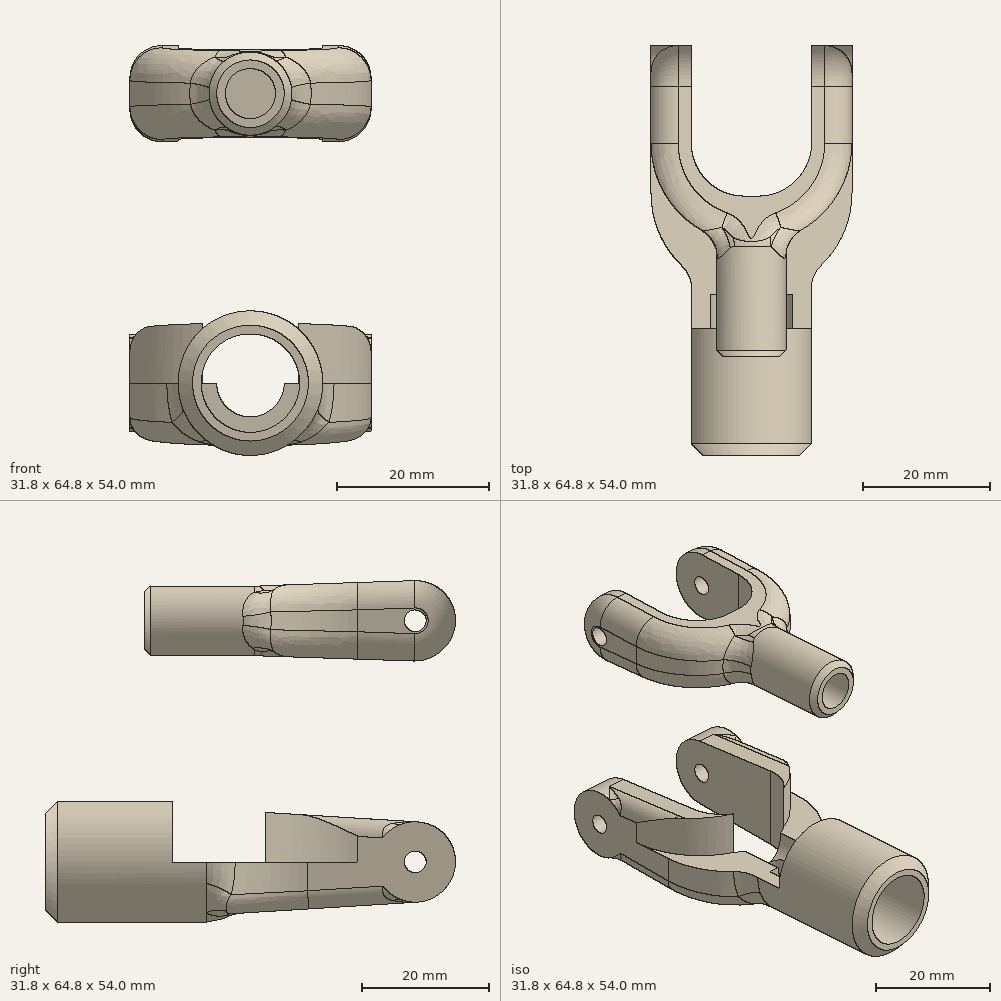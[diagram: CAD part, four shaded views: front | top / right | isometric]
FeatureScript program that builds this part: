
annotation { "Feature Type Name" : "Feature", "Feature Type Description" : "" }
export const myFeature = defineFeature(function(context is Context, id is Id, definition is map)
    precondition{}
    {
        {
            var Q0;
            Q0=qCreatedBy(makeId("Right.planeOp"),FACE);
            var sketch = newSketch(context, id + "F0", { "sketchPlane" : qUnion([Q0])});
            skArc(sketch, "E0", {"start": v(0.4, -6.34) * mm, "mid": v(6.35, 0) * mm, "end": v(0.4, 6.34) * mm});
            skLineSegment(sketch, "E1", {"start": v(0.4, 6.34) * mm, "end": v(-50.8, 9.52) * mm});
            skLineSegment(sketch, "E2", {"start": v(-50.8, 9.52) * mm, "end": v(-50.8, -9.52) * mm});
            skLineSegment(sketch, "E3", {"start": v(-50.8, -9.52) * mm, "end": v(0.4, -6.34) * mm});
            skCircle(sketch, "E4", {"center": v(0, 0) * mm, "radius": 1.71 * mm});
            skSolve(sketch);
        }
        {
            var Q0;
            Q0=qSketchRegion(id+"F0",true);
            extrude(context, id + "F1", {"entities" : qUnion([Q0]), "depth" : 15.88 * mm, "hasSecondDirection" : true, "secondDirectionOppositeDirection" : true, "secondDirectionDepth" : 15.88 * mm});
        }
        {
            var Q0;
            Q0=qCreatedBy(makeId("Top.planeOp"),FACE);
            var sketch = newSketch(context, id + "F2", { "sketchPlane" : qUnion([Q0])});
            skLineSegment(sketch, "E5.bottom", {"start": v(-9.52, 7.24) * mm, "end": v(9.52, 7.24) * mm});
            skLineSegment(sketch, "E5.top", {"start": v(-1.14, -25.4) * mm, "end": v(1.14, -25.4) * mm});
            skLineSegment(sketch, "E5.left", {"start": v(-9.52, 7.24) * mm, "end": v(-9.52, -17.02) * mm});
            skLineSegment(sketch, "E5.right", {"start": v(9.53, 7.24) * mm, "end": v(9.53, -17.02) * mm});
            skPoint(sketch, "E6.visualSharp", {"position": v(-9.52, -25.4) * mm});
            skArc(sketch, "E6.filletArc", {"start": v(-9.52, -17.02) * mm, "mid": v(-7.07, -22.94) * mm, "end": v(-1.14, -25.4) * mm});
            skPoint(sketch, "E7.visualSharp", {"position": v(9.52, -25.4) * mm});
            skArc(sketch, "E7.filletArc", {"start": v(1.14, -25.4) * mm, "mid": v(7.07, -22.94) * mm, "end": v(9.52, -17.02) * mm});
            skArc(sketch, "E8", {"start": v(-15.88, -17.02) * mm, "mid": v(0, -32.9) * mm, "end": v(15.88, -17.02) * mm});
            skLineSegment(sketch, "E9", {"start": v(-15.88, -17.02) * mm, "end": v(-15.88, -50.8) * mm});
            skLineSegment(sketch, "E10", {"start": v(-15.88, -50.8) * mm, "end": v(15.88, -50.8) * mm});
            skLineSegment(sketch, "E11", {"start": v(15.88, -50.8) * mm, "end": v(15.88, -17.02) * mm});
            skSolve(sketch);
        }
        {
            var Q0;
            Q0=qSketchRegion(id+"F2",true);
            extrude(context, id + "F3", {"entities" : qUnion([Q0]), "operationType" : NewBodyOperationType.REMOVE, "endBound" : BoundingType.THROUGH_ALL, "oppositeDirection" : true, "depth" : 25.4 * mm, "hasSecondDirection" : true, "secondDirectionBound" : BoundingType.THROUGH_ALL, "secondDirectionOppositeDirection" : false, "secondDirectionDepth" : 25.4 * mm});
        }
        {
            var Q0;
            Q0=qCreatedBy(makeId("Right.planeOp"),FACE);
            var sketch = newSketch(context, id + "F4", { "sketchPlane" : qUnion([Q0])});
            skLineSegment(sketch, "E12", {"start": v(0, 0) * mm, "end": v(-108.54, 0) * mm, "construction": true});
            skSolve(sketch);
        }
        {
            var Q0;
            Q0=qCreatedBy(makeId("Right.planeOp"),FACE);
            var sketch = newSketch(context, id + "F5", { "sketchPlane" : qUnion([Q0])});
            skLineSegment(sketch, "E13", {"start": v(-25.4, 0) * mm, "end": v(-25.4, 7.94) * mm});
            skLineSegment(sketch, "E14", {"start": v(-58.42, 9.53) * mm, "end": v(-58.42, 0) * mm});
            skLineSegment(sketch, "E15", {"start": v(-58.42, 0) * mm, "end": v(-25.4, 0) * mm});
            skLineSegment(sketch, "E16", {"start": v(-25.4, 7.94) * mm, "end": v(-33.02, 9.53) * mm});
            skLineSegment(sketch, "E17", {"start": v(-33.02, 9.53) * mm, "end": v(-58.42, 9.53) * mm});
            skSolve(sketch);
        }
        {
            var Q0;
            Q0=qSketchRegion(id+"F5",true);
            var Q1;
            Q1=sQuery(id+"F4.wireOp",EDGE,"E12");
            revolve(context, id + "F6", {"operationType" : NewBodyOperationType.ADD, "entities" : qUnion([Q0]), "axis" : qUnion([Q1]), "revolveType" : RevolveType.FULL});
        }
        {
            var Q0;
            Q0=qCreatedBy(makeId("Right.planeOp"),FACE);
            var sketch = newSketch(context, id + "F7", { "sketchPlane" : qUnion([Q0])});
            skLineSegment(sketch, "E18", {"start": v(-58.42, 6.48) * mm, "end": v(-33.02, 6.48) * mm});
            skLineSegment(sketch, "E19", {"start": v(-33.02, 6.48) * mm, "end": v(-33.02, 4.45) * mm});
            skLineSegment(sketch, "E20", {"start": v(-33.02, 4.45) * mm, "end": v(-23.5, 4.45) * mm});
            skLineSegment(sketch, "E21", {"start": v(-23.5, 4.45) * mm, "end": v(-23.5, 0) * mm});
            skLineSegment(sketch, "E22", {"start": v(-58.42, 6.48) * mm, "end": v(-58.42, 0) * mm});
            skLineSegment(sketch, "E23", {"start": v(-58.42, 0) * mm, "end": v(-23.5, 0) * mm});
            skSolve(sketch);
        }
        {
            var Q0;
            Q0=qSketchRegion(id+"F7",true);
            var Q1;
            Q1=sQuery(id+"F4.wireOp",EDGE,"E12");
            revolve(context, id + "F8", {"operationType" : NewBodyOperationType.REMOVE, "entities" : qUnion([Q0]), "axis" : qUnion([Q1]), "revolveType" : RevolveType.FULL, "oppositeDirection" : true});
        }
        {
            var Q0;
            {var subQ0=sQuery(id+"F0.wireOp",EDGE,"E1");var subQ1=makeQuery(id+"F1.opExtrude","SWEPT_FACE",FACE,{"disambiguationData":[OSD([subQ0])]});var subQ2=makeQuery(id+"F3.opExtrude","SWEPT_FACE",FACE,{"disambiguationData":[OSD([sQuery(id+"F2.wireOp",EDGE,"E8")])]});Q0=makeQuery(id+"F6.boolean.opBoolean","SPLIT",EDGE,{"disambiguationData":[TD([makeQuery(id+"F1.opExtrude","CAP_FACE",FACE,{"disambiguationData":[OSD([sQuery(id+"F0.wireOp",EDGE,"E0"),subQ0,sQuery(id+"F0.wireOp",EDGE,"E2"),sQuery(id+"F0.wireOp",EDGE,"E3"),sQuery(id+"F0.wireOp",EDGE,"E4")])],"isStart":true})])],"derivedFrom":makeQuery(id+"F3.boolean.opBoolean","INTERSECT",EDGE,{"derivedFrom":[subQ1,subQ2]})});}
            var Q1;
            {var subQ0=sQuery(id+"F0.wireOp",EDGE,"E1");var subQ1=makeQuery(id+"F1.opExtrude","SWEPT_FACE",FACE,{"disambiguationData":[OSD([subQ0])]});var subQ2=makeQuery(id+"F3.opExtrude","SWEPT_FACE",FACE,{"disambiguationData":[OSD([sQuery(id+"F2.wireOp",EDGE,"E8")])]});Q1=makeQuery(id+"F6.boolean.opBoolean","SPLIT",EDGE,{"disambiguationData":[TD([makeQuery(id+"F1.opExtrude","CAP_FACE",FACE,{"disambiguationData":[OSD([sQuery(id+"F0.wireOp",EDGE,"E0"),subQ0,sQuery(id+"F0.wireOp",EDGE,"E2"),sQuery(id+"F0.wireOp",EDGE,"E3"),sQuery(id+"F0.wireOp",EDGE,"E4")])],"isStart":false})])],"derivedFrom":makeQuery(id+"F3.boolean.opBoolean","INTERSECT",EDGE,{"derivedFrom":[subQ1,subQ2]})});}
            fillet(context, id + "F9", {"entities" : qUnion([Q0, Q1]), "radius" : 2.87 * mm, "tangentPropagation" : true, "allowEdgeOverflow" : false});
        }
        {
            var Q0;
            Q0=makeQuery(id+"F6.boolean.opBoolean","INTERSECT",EDGE,{"disambiguationData":[OD(1.0)],"derivedFrom":[makeQuery(id+"F3.boolean.opBoolean","COPY",FACE,{"derivedFrom":makeQuery(id+"F3.opExtrude","SWEPT_FACE",FACE,{"disambiguationData":[OSD([sQuery(id+"F2.wireOp",EDGE,"E8")])]})}),makeQuery(id+"F6.opRevolve","SWEPT_FACE",FACE,{"disambiguationData":[OSD([sQuery(id+"F5.wireOp",EDGE,"E16")])]})]});
            fillet(context, id + "F10", {"entities" : qUnion([Q0]), "radius" : 5.08 * mm, "tangentPropagation" : true, "allowEdgeOverflow" : false});
        }
        {
            var Q0;
            Q0=makeQuery(id+"F6.opRevolve","SWEPT_EDGE",EDGE,{"disambiguationData":[OSD([sQuery(id+"F5.wireOp",EDGE,"E14"),sQuery(id+"F5.wireOp",EDGE,"E17")])]});
            chamfer(context, id + "F11", {"entities" : qUnion([Q0]), "width" : 1.9 * mm, "tangentPropagation" : true});
        }
        {
            var Q0;
            Q0=qCreatedBy(makeId("Right.planeOp"),FACE);
            var sketch = newSketch(context, id + "F12", { "sketchPlane" : qUnion([Q0])});
            skCircle(sketch, "E24", {"center": v(0, 38.1) * mm, "radius": 1.71 * mm});
            skArc(sketch, "E25", {"start": v(-0.21, 31.75) * mm, "mid": v(6.35, 38.1) * mm, "end": v(-0.21, 44.45) * mm});
            skLineSegment(sketch, "E26", {"start": v(-0.21, 44.45) * mm, "end": v(-38.3, 43.18) * mm});
            skLineSegment(sketch, "E27", {"start": v(-38.3, 43.18) * mm, "end": v(-38.3, 33.02) * mm});
            skLineSegment(sketch, "E28", {"start": v(-38.3, 33.02) * mm, "end": v(-0.21, 31.75) * mm});
            skLineSegment(sketch, "E29", {"start": v(-60.22, 38.1) * mm, "end": v(0, 38.1) * mm, "construction": true});
            skSolve(sketch);
        }
        {
            var Q0;
            Q0=qSketchRegion(id+"F12",true);
            extrude(context, id + "F13", {"entities" : qUnion([Q0]), "depth" : 15.88 * mm, "hasSecondDirection" : true, "secondDirectionOppositeDirection" : true, "secondDirectionDepth" : 15.88 * mm});
        }
        {
            var Q0;
            Q0=qCreatedBy(makeId("Top.planeOp"),FACE);
            var sketch = newSketch(context, id + "F14", { "sketchPlane" : qUnion([Q0])});
            skLineSegment(sketch, "E30.bottom", {"start": v(-9.53, 7.96) * mm, "end": v(9.53, 7.96) * mm});
            skLineSegment(sketch, "E30.top", {"start": v(-1.14, -17.44) * mm, "end": v(1.14, -17.44) * mm});
            skLineSegment(sketch, "E30.left", {"start": v(-9.53, 7.96) * mm, "end": v(-9.53, -9.06) * mm});
            skLineSegment(sketch, "E30.right", {"start": v(9.53, 7.96) * mm, "end": v(9.53, -9.06) * mm});
            skPoint(sketch, "E31.visualSharp", {"position": v(-9.53, -17.44) * mm});
            skArc(sketch, "E31.filletArc", {"start": v(-9.53, -9.06) * mm, "mid": v(-7.07, -14.99) * mm, "end": v(-1.14, -17.44) * mm});
            skPoint(sketch, "E32.visualSharp", {"position": v(9.53, -17.44) * mm});
            skArc(sketch, "E32.filletArc", {"start": v(1.14, -17.44) * mm, "mid": v(7.07, -14.99) * mm, "end": v(9.53, -9.06) * mm});
            skArc(sketch, "E33", {"start": v(-15.88, -9.06) * mm, "mid": v(0, -24.94) * mm, "end": v(15.88, -9.06) * mm});
            skLineSegment(sketch, "E34", {"start": v(-15.88, -9.06) * mm, "end": v(-15.88, -38.3) * mm});
            skLineSegment(sketch, "E35", {"start": v(-15.88, -38.3) * mm, "end": v(15.88, -38.3) * mm});
            skLineSegment(sketch, "E36", {"start": v(15.88, -38.3) * mm, "end": v(15.88, -9.06) * mm});
            skSolve(sketch);
        }
        {
            var Q0;
            Q0=qSketchRegion(id+"F14",true);
            extrude(context, id + "F15", {"entities" : qUnion([Q0]), "operationType" : NewBodyOperationType.REMOVE, "endBound" : BoundingType.THROUGH_ALL, "depth" : 25.4 * mm});
        }
        {
            var Q0;
            Q0=makeQuery(id+"F15.boolean.opBoolean","COPY",FACE,{"derivedFrom":makeQuery(id+"F15.opExtrude","SWEPT_FACE",FACE,{"disambiguationData":[OSD([sQuery(id+"F14.wireOp",EDGE,"E30.top")])]})});
            var sketch = newSketch(context, id + "F16", { "sketchPlane" : qUnion([Q0])});
            skCircle(sketch, "E37", {"center": v(0, 38.1) * mm, "radius": 5.46 * mm});
            skSolve(sketch);
        }
        {
            var Q0;
            Q0=qSketchRegion(id+"F16",true);
            extrude(context, id + "F17", {"entities" : qUnion([Q0]), "operationType" : NewBodyOperationType.ADD, "oppositeDirection" : true, "depth" : 25.4 * mm});
        }
        {
            var Q0;
            Q0=makeQuery(id+"F17.opExtrude","CAP_FACE",FACE,{"disambiguationData":[OSD([sQuery(id+"F16.wireOp",EDGE,"E37")])],"isStart":false});
            var sketch = newSketch(context, id + "F18", { "sketchPlane" : qUnion([Q0])});
            skCircle(sketch, "E38", {"center": v(0, 38.1) * mm, "radius": 3.3 * mm});
            skSolve(sketch);
        }
        {
            var Q0;
            Q0=qSketchRegion(id+"F18",true);
            extrude(context, id + "F19", {"entities" : qUnion([Q0]), "operationType" : NewBodyOperationType.REMOVE, "oppositeDirection" : true, "depth" : 22.86 * mm});
        }
        {
            var Q0;
            Q0=makeQuery(id+"F17.opExtrude","CAP_EDGE",EDGE,{"disambiguationData":[OSD([sQuery(id+"F16.wireOp",EDGE,"E37")])],"isStart":false});
            chamfer(context, id + "F20", {"entities" : qUnion([Q0]), "width" : 1.02 * mm, "tangentPropagation" : true});
        }
        {
            var Q0;
            Q0=makeQuery(id+"F13.opExtrude","CAP_EDGE",EDGE,{"disambiguationData":[OSD([sQuery(id+"F12.wireOp",EDGE,"E26")])],"isStart":true});
            fillet(context, id + "F21", {"entities" : qUnion([Q0]), "radius" : 4.32 * mm, "tangentPropagation" : true, "allowEdgeOverflow" : false});
        }
        {
            var Q0;
            Q0=makeQuery(id+"F1.opExtrude","CAP_FACE",FACE,{"disambiguationData":[OSD([sQuery(id+"F0.wireOp",EDGE,"E0"),sQuery(id+"F0.wireOp",EDGE,"E1"),sQuery(id+"F0.wireOp",EDGE,"E2"),sQuery(id+"F0.wireOp",EDGE,"E3"),sQuery(id+"F0.wireOp",EDGE,"E4")])],"isStart":true});
            var sketch = newSketch(context, id + "F22", { "sketchPlane" : qUnion([Q0])});
            skCircle(sketch, "E39", {"center": v(0, 0) * mm, "radius": 6.35 * mm});
            skCircle(sketch, "E40", {"center": v(0, 0) * mm, "radius": 1.71 * mm});
            skSolve(sketch);
        }
        {
            var Q0;
            Q0=qSketchRegion(id+"F22",true);
            extrude(context, id + "F23", {"entities" : qUnion([Q0]), "operationType" : NewBodyOperationType.ADD, "oppositeDirection" : true, "depth" : 5.08 * mm});
        }
        {
            var Q0;
            Q0=makeQuery(id+"F1.opExtrude","CAP_FACE",FACE,{"disambiguationData":[OSD([sQuery(id+"F0.wireOp",EDGE,"E0"),sQuery(id+"F0.wireOp",EDGE,"E1"),sQuery(id+"F0.wireOp",EDGE,"E2"),sQuery(id+"F0.wireOp",EDGE,"E3"),sQuery(id+"F0.wireOp",EDGE,"E4")])],"isStart":false});
            var sketch = newSketch(context, id + "F24", { "sketchPlane" : qUnion([Q0])});
            skCircle(sketch, "E41", {"center": v(0, 0) * mm, "radius": 6.35 * mm});
            skCircle(sketch, "E42", {"center": v(0, 0) * mm, "radius": 1.71 * mm});
            skSolve(sketch);
        }
        {
            var Q0;
            Q0=qSketchRegion(id+"F24",true);
            extrude(context, id + "F25", {"entities" : qUnion([Q0]), "operationType" : NewBodyOperationType.ADD, "oppositeDirection" : true, "depth" : 5.08 * mm});
        }
        {
            var Q0;
            Q0=makeQuery(id+"F21.opFillet","BLEND_EDGE",EDGE,{"blendedFrom":[makeQuery(id+"F15.boolean.opBoolean","INTERSECT",EDGE,{"derivedFrom":[makeQuery(id+"F13.opExtrude","SWEPT_FACE",FACE,{"disambiguationData":[OSD([sQuery(id+"F12.wireOp",EDGE,"E26")])]}),makeQuery(id+"F15.opExtrude","SWEPT_FACE",FACE,{"disambiguationData":[OSD([sQuery(id+"F14.wireOp",EDGE,"E33")])]})]}),makeQuery(id+"F17.opExtrude","SWEPT_FACE",FACE,{"disambiguationData":[OSD([sQuery(id+"F16.wireOp",EDGE,"E37")])]})],"blendedInto":[makeQuery(id+"F17.opExtrude","SWEPT_FACE",FACE,{"disambiguationData":[OSD([sQuery(id+"F16.wireOp",EDGE,"E37")])]})]});
            fillet(context, id + "F26", {"entities" : qUnion([Q0]), "radius" : 5.08 * mm, "tangentPropagation" : true, "allowEdgeOverflow" : false});
        }
        {
            var Q0;
            {var subQ0=sQuery(id+"F0.wireOp",EDGE,"E1");Q0=makeQuery(id+"F25.boolean.opBoolean","INTERSECT",EDGE,{"derivedFrom":[makeQuery(id+"F9.opFillet","BLEND_FACE",FACE,{"disambiguationData":[OSD([subQ0]),TDD([makeQuery(id+"F1.opExtrude","CAP_EDGE",EDGE,{"disambiguationData":[OSD([subQ0])],"isStart":false})])]}),makeQuery(id+"F25.opExtrude","SWEPT_FACE",FACE,{"disambiguationData":[OSD([sQuery(id+"F24.wireOp",EDGE,"E41")])]})]});}
            var Q1;
            {var subQ0=sQuery(id+"F0.wireOp",EDGE,"E3");Q1=makeQuery(id+"F25.boolean.opBoolean","INTERSECT",EDGE,{"derivedFrom":[makeQuery(id+"F9.opFillet","BLEND_FACE",FACE,{"disambiguationData":[OSD([subQ0]),TDD([makeQuery(id+"F1.opExtrude","CAP_EDGE",EDGE,{"disambiguationData":[OSD([subQ0])],"isStart":false})])]}),makeQuery(id+"F25.opExtrude","SWEPT_FACE",FACE,{"disambiguationData":[OSD([sQuery(id+"F24.wireOp",EDGE,"E41")])]})]});}
            var Q2;
            {var subQ0=sQuery(id+"F0.wireOp",EDGE,"E3");Q2=makeQuery(id+"F23.boolean.opBoolean","INTERSECT",EDGE,{"derivedFrom":[makeQuery(id+"F9.opFillet","BLEND_FACE",FACE,{"disambiguationData":[OSD([subQ0]),TDD([makeQuery(id+"F1.opExtrude","CAP_EDGE",EDGE,{"disambiguationData":[OSD([subQ0])],"isStart":true})])]}),makeQuery(id+"F23.opExtrude","SWEPT_FACE",FACE,{"disambiguationData":[OSD([sQuery(id+"F22.wireOp",EDGE,"E39")])]})]});}
            var Q3;
            {var subQ0=sQuery(id+"F0.wireOp",EDGE,"E1");Q3=makeQuery(id+"F23.boolean.opBoolean","INTERSECT",EDGE,{"derivedFrom":[makeQuery(id+"F9.opFillet","BLEND_FACE",FACE,{"disambiguationData":[OSD([subQ0]),TDD([makeQuery(id+"F1.opExtrude","CAP_EDGE",EDGE,{"disambiguationData":[OSD([subQ0])],"isStart":true})])]}),makeQuery(id+"F23.opExtrude","SWEPT_FACE",FACE,{"disambiguationData":[OSD([sQuery(id+"F22.wireOp",EDGE,"E39")])]})]});}
            fillet(context, id + "F27", {"entities" : qUnion([Q0, Q1, Q2, Q3]), "radius" : 2.54 * mm, "tangentPropagation" : true, "allowEdgeOverflow" : false});
        }
        {
            var Q0;
            Q0=qCreatedBy(makeId("Top.planeOp"),FACE);
            var sketch = newSketch(context, id + "F28", { "sketchPlane" : qUnion([Q0])});
            skCircle(sketch, "E43", {"center": v(0, -27.69) * mm, "radius": 2.54 * mm});
            skSolve(sketch);
        }
        {
            var Q0;
            Q0=qSketchRegion(id+"F28",true);
            extrude(context, id + "F29", {"entities" : qUnion([Q0]), "operationType" : NewBodyOperationType.REMOVE, "endBound" : BoundingType.THROUGH_ALL, "oppositeDirection" : true, "depth" : 25.4 * mm});
        }
    });
